# Revit family: Network Camera-PTZ-Q-SYS-NC-Pro15x
name_source: partatom
category: Communication Devices
units: mm (PartAtom-declared; Revit-internal decimal feet)

## family parameters
Cut with Voids When Loaded = No
Host = Face
Maintain Annotation Orientation = No
OmniClass Number = 23.85.10.14.11
OmniClass Title = Cameras
Part Type = Normal
Room Calculation Point = No
Round Connector Dimension = Use Diameter
Shared = No

## types (2) — shared parameters
Angle 1 = 86.00°
Assembly Code = E1020500
Base Height = 100 mm  [stored 0.328084 ft]
Body Radius 1 = 100 mm  [stored 0.328084 ft]
Body Radius 2 = 93 mm  [stored 0.305118 ft]
Camera Front to Center = 73 mm  [stored 0.239501 ft]
Camera Half Height = 45 mm
Camera Half Width = 40 mm  [stored 0.131234 ft]
Coverage Horizontal = 340.00°
Coverage Vertical = 120.00°
Default Elevation = 1219 mm
Depth = 218 mm  [stored 0.715223 ft]
Description = Network camera with motorized PTZ, 15x optical zoom (20x digital) and 73° horizontal FoV.
Height = 269 mm
Highlight Material = Glass - Q-SYS - Lens
IQ Category = Network Camera
Length 1 = 123 mm
Manufacturer = Q-SYS
Manufacturer URL = https://www.qsys.com
Model = NC-Pro15x
Offset = 279 mm
OmniClass Number = 23.85.10.14.11
Part Number = NC-Pro15x
Product Documentation Link = https://www.qsys.com
Product Page URL = https://www.qsys.com
Trim Material = Paint - Q-SYS - Black
URL = https://www.qsys.com
Voltage DC = PoE+ (Type 2)
Weight = 9.04 lbm
Weight Dimensional = 9.04
Weight Product = 9.04
Width = 200 mm  [stored 0.656168 ft]
zero-valued in all types: Length 2

## per-type parameters (varying)
| type | Body Material |
| White | Paint - Q-SYS - White |
| Black | Paint - Q-SYS - Black |

note: column(s) folded — value = type name in every type: Type Comments

note: [stored X ft] marks values corroborated as IEEE doubles in the binary element streams (Revit-internal decimal feet)

## geometry (parser evidence)
native form markers: Sweep x3
no freeform markers — native parametric forms only
